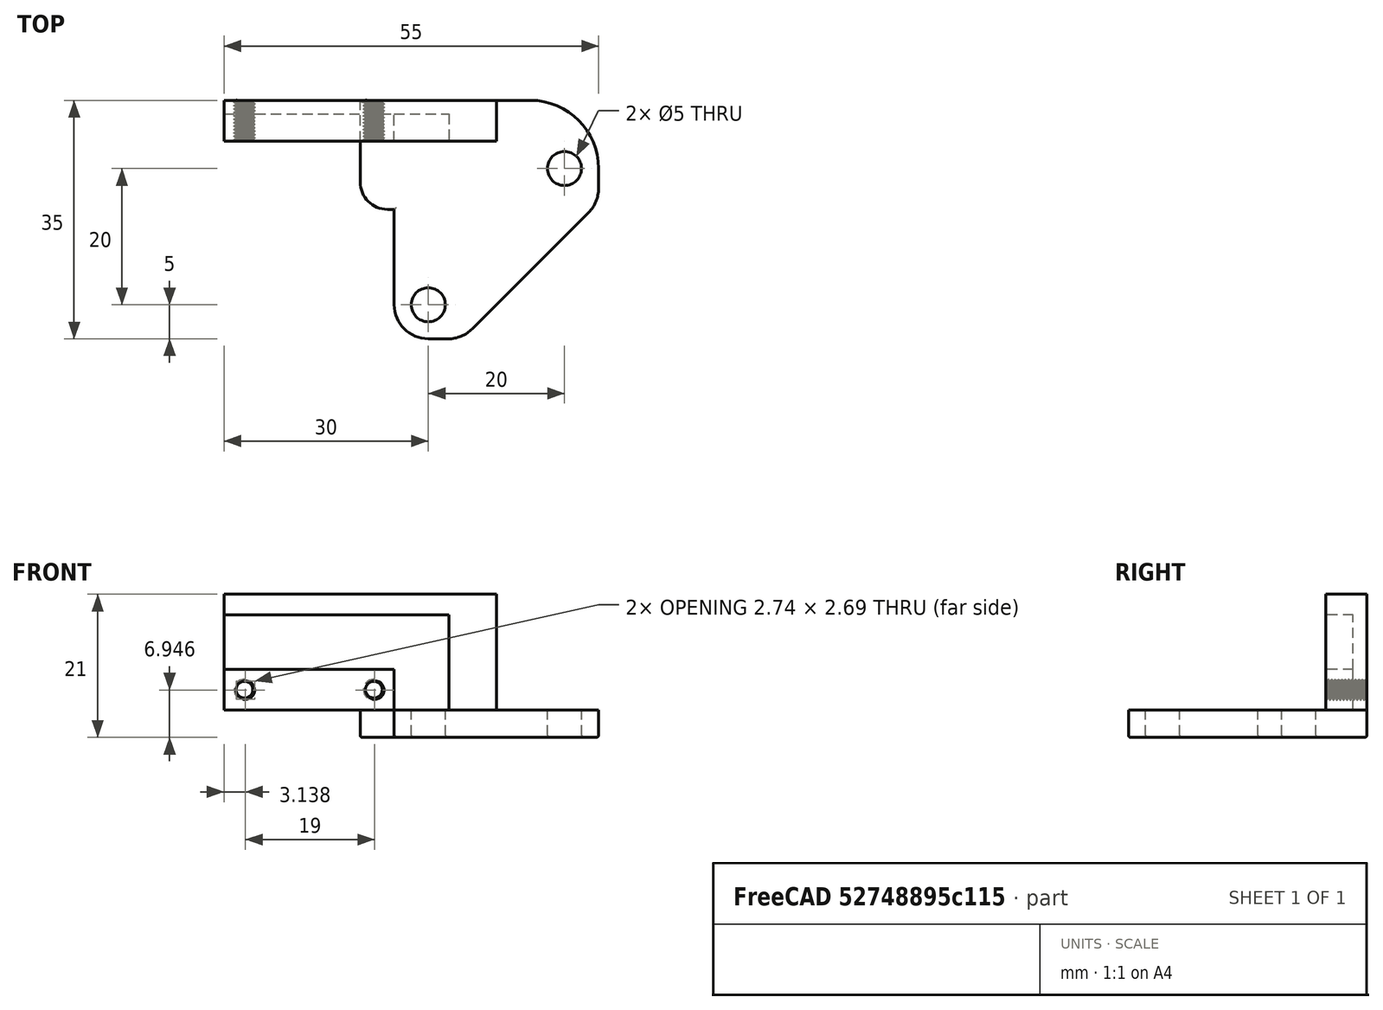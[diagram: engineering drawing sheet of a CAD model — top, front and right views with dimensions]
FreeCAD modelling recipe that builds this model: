
FCSTD DOCUMENT  (FreeCAD 0.18R16146 (Git))
Label: Y_DriveEndschalter_links_Ver3
License: All rights reserved
LicenseURL: http://en.wikipedia.org/wiki/All_rights_reserved
objects: Part::Cut×8, Part::Box×6, Part::Fillet×4, Part::Feature×2, Part::Cylinder×2, Part::Chamfer×1, Part::Mirroring×1, Part::MultiFuse×1
note: 25 computed .brp shape members not serialized (recipe doc carries the construction recipe); baked Part::Feature solids carry a one-line shape summary decoded from their .brp

FEATURE [Part::Box] Box  label="Cube"
  AttacherType = Attacher::AttachEngine3D
  Height = 6
  Length = 40
  Width = 17
FEATURE [Part::Box] Box001  label="Cube001"
  AttacherType = Attacher::AttachEngine3D
  Height = 10
  Length = 33
  Placement = pos=(0,6,2) rot=(0,0,1;0rad)
  Width = 8
FEATURE [Part::Box] Box002  label="Cube002"
  AttacherType = Attacher::AttachEngine3D
  Height = 10
  Length = 8
  Placement = pos=(25,0,2) rot=(0,0,1;0rad)
  Width = 14
FEATURE [Part::Feature] Part__Feature  label="ScrewTap-M3x50_"
  Placement = pos=(3,3,8) rot=(0,0,1;0rad)
  shape: bbox 4.303 x 4.617 x 51.5 mm, 410 faces (baked)
FEATURE [Part::Feature] Part__Feature001  label="ScrewTap-M3x50_001"
  Placement = pos=(22,3,8) rot=(0,0,1;0rad)
  shape: bbox 4.303 x 4.617 x 51.5 mm, 410 faces (baked)
FEATURE [Part::Cut] Cut
  Base = -> Box
  Tool = -> Box001
FEATURE [Part::Cut] Cut001
  Base = -> Cut
  Tool = -> Box002
FEATURE [Part::Cut] Cut002
  Base = -> Cut001
  Tool = -> Part__Feature001
FEATURE [Part::Cut] Cut003
  Base = -> Cut002
  Placement = pos=(-10,16,4) rot=(1,0,0;1.5708rad)
  Tool = -> Part__Feature
FEATURE [Part::Box] Box003  label="Cube003"
  AttacherType = Attacher::AttachEngine3D
  Height = 4
  Length = 45
  Width = 35
FEATURE [Part::Cylinder] Cylinder
  Angle = 360
  AttacherType = Attacher::AttachEngine3D
  Height = 10
  Placement = pos=(40,10,0) rot=(0,0,1;0rad)
  Radius = 2.5
FEATURE [Part::Cylinder] Cylinder001
  Angle = 360
  AttacherType = Attacher::AttachEngine3D
  Height = 10
  Placement = pos=(20,30,0) rot=(0,0,1;0rad)
  Radius = 2.5
FEATURE [Part::Box] Box004  label="Cube004"
  AttacherType = Attacher::AttachEngine3D
  Height = 10
  Length = 15
  Placement = pos=(0,16,0) rot=(0,0,1;0rad)
  Width = 19
FEATURE [Part::Cut] Cut004
  Base = -> Box003
  Tool = -> Box004
FEATURE [Part::Chamfer] Chamfer
  Base = -> Cut004
  Edges = 1 edges r=20: [Edge18]
FEATURE [Part::Fillet] Fillet
  Base = -> Chamfer
  Edges = 2 edges r=10: [Edge15,Edge20]
FEATURE [Part::Fillet] Fillet001
  Base = -> Fillet
  Edges = 3 edges r=5: [Edge11,Edge16,Edge20]
FEATURE [Part::Cut] Cut005
  Base = -> Fillet001
  Tool = -> Cylinder001
FEATURE [Part::Cut] Cut006
  Base = -> Cut005
  Tool = -> Cylinder
FEATURE [Part::Mirroring] Part__Mirroring  label="Cut006 (Mirror #1)"
  Base = (0,0,0)
  Normal = (0,1,0)
  Placement = pos=(0,16,0) rot=(0,0,1;0rad)
  Source = -> Cut006
FEATURE [Part::Box] Box005  label="Cube005"
  AttacherType = Attacher::AttachEngine3D
  Height = 4
  Length = 10
  Width = 16
FEATURE [Part::Cut] Cut007
  Base = -> Part__Mirroring
  Tool = -> Box005
FEATURE [Part::Fillet] Fillet002
  Base = -> Cut007
  Edges = 1 edges r=4: [Edge21]
FEATURE [Part::Fillet] Fillet003
  Base = -> Fillet002
  Edges = 14 edges r=0.3: [Edge17,Edge18,Edge20,Edge23,Edge24,Edge27,Edge29,Edge30,Edge32,Edge34,Edge36,Edge38,Edge40,Edge42]
FEATURE [Part::MultiFuse] Fusion
  Shapes = -> [Cut003,Fillet003]
